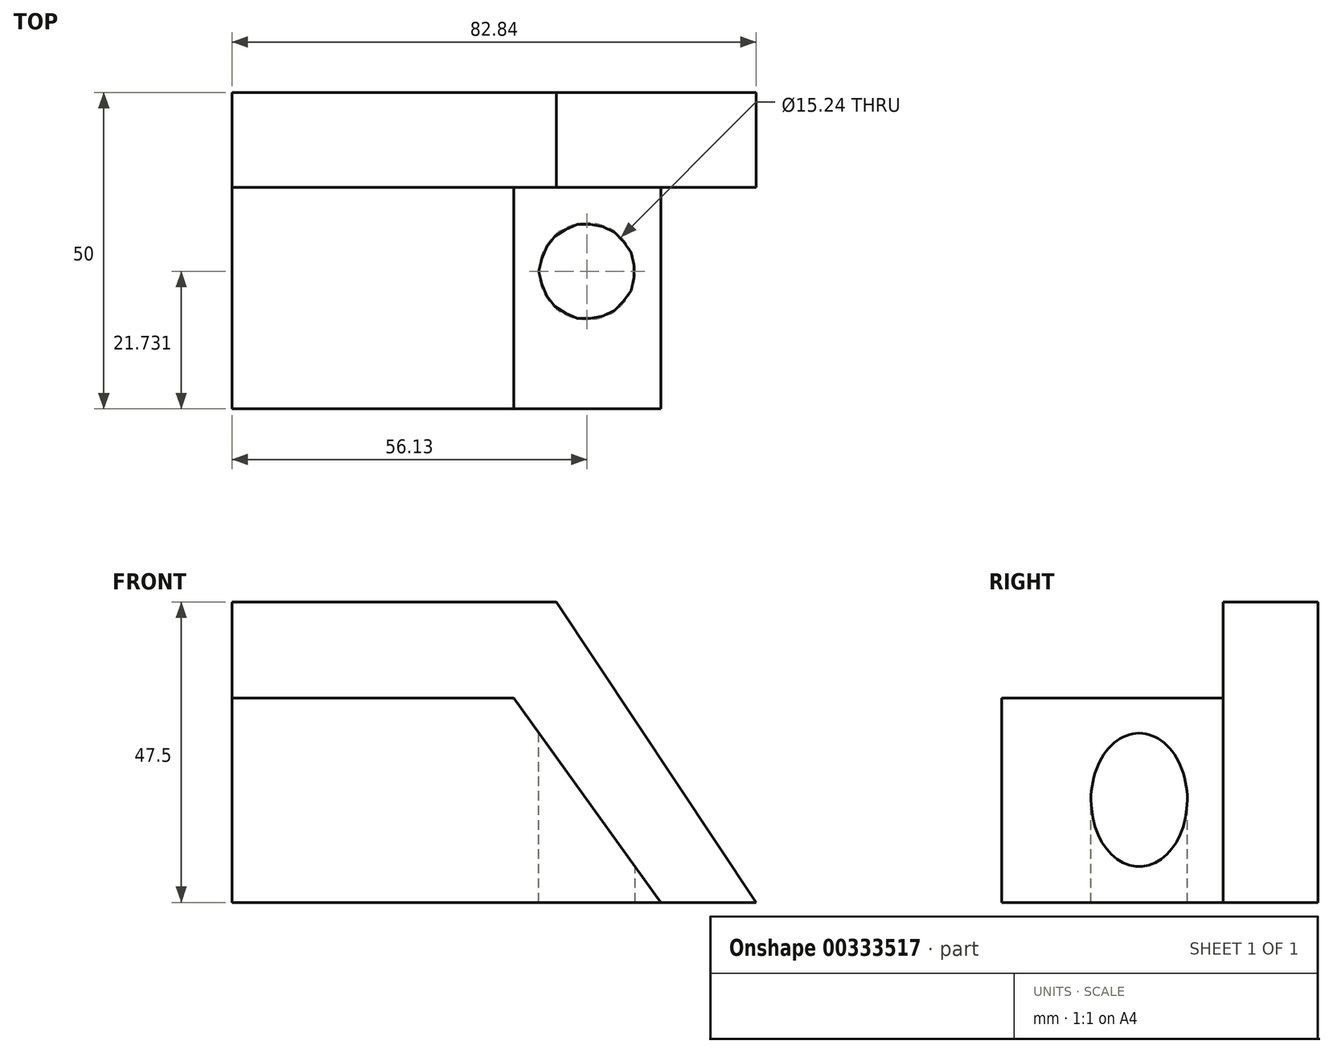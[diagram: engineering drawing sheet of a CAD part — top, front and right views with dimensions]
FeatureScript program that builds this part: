
annotation { "Feature Type Name" : "Feature", "Feature Type Description" : "" }
export const myFeature = defineFeature(function(context is Context, id is Id, definition is map)
    precondition{}
    {
        {
            var Q0;
            Q0=qCreatedBy(makeId("Front.planeOp"),FACE);
            var sketch = newSketch(context, id + "F0", { "sketchPlane" : qUnion([Q0])});
            skLineSegment(sketch, "E0", {"start": v(0, 0) * mm, "end": v(0, 32.3) * mm});
            skLineSegment(sketch, "E1", {"start": v(0, 32.3) * mm, "end": v(44.52, 32.3) * mm});
            skLineSegment(sketch, "E2", {"start": v(44.52, 32.3) * mm, "end": v(67.79, 0) * mm});
            skLineSegment(sketch, "E3", {"start": v(67.79, 0) * mm, "end": v(0, 0) * mm});
            skSolve(sketch);
        }
        {
            var Q0;
            Q0 = qSketchRegion(id + "F0", true);
            extrude(context, id + "F1", {"entities" : qUnion([Q0]), "depth" : 50 * mm, "offsetDistance" : 25 * mm});
        }
        {
            var Q0;
            Q0=qCreatedBy(makeId("Front.planeOp"),FACE);
            var sketch = newSketch(context, id + "F2", { "sketchPlane" : qUnion([Q0])});
            skLineSegment(sketch, "E4", {"start": v(0, 0) * mm, "end": v(82.84, 0) * mm});
            skLineSegment(sketch, "E5", {"start": v(82.84, 0) * mm, "end": v(51.3, 47.5) * mm});
            skLineSegment(sketch, "E6", {"start": v(51.3, 47.5) * mm, "end": v(0, 47.5) * mm});
            skLineSegment(sketch, "E7", {"start": v(0, 47.5) * mm, "end": v(0, 0) * mm});
            skSolve(sketch);
        }
        {
            var Q0;
            Q0 = qSketchRegion(id + "F2", true);
            extrude(context, id + "F3", {"entities" : qUnion([Q0]), "operationType" : NewBodyOperationType.ADD, "depth" : 15 * mm, "offsetDistance" : 25 * mm});
        }
        {
            var Q0;
            Q0=qCreatedBy(makeId("Top.planeOp"),FACE);
            var sketch = newSketch(context, id + "F4", { "sketchPlane" : qUnion([Q0])});
            skCircle(sketch, "E8", {"center": v(56.13, -28.27) * mm, "radius": 7.62 * mm});
            skSolve(sketch);
        }
        {
            var Q0;
            Q0 = qSketchRegion(id + "F4", true);
            extrude(context, id + "F5", {"entities" : qUnion([Q0]), "operationType" : NewBodyOperationType.REMOVE, "oppositeDirection" : true, "depth" : 590 * mm, "offsetDistance" : 25 * mm, "symmetric" : true});
        }
    });
